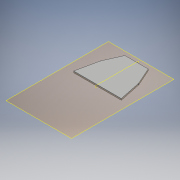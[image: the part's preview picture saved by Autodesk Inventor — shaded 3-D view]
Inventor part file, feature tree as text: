
AUTODESK INVENTOR PART (.ipt)
format: ipt  version: 2018 (Build 220112000, 112)  size: 160,256 bytes
history: native  units: mm
features: other x8, plane x1, sheet_metal_op x1, sketch x1, projected_geometry x1
ambient origin geometry x8: Origin, YZ Plane, XZ Plane, XY Plane, X Axis, Y Axis, Z Axis, Center Point
bodies: Solid1 (feature_tree)
feature tree (12):
  plane  "Work Plane1"
  sheet_metal_op  "Face1"
  other  "modplan parallel med plade"
  other  "midtplan"
  other  "Plate1"
  sketch  "Sketch3"  dims[d3=88.078826mm d4=44.039413mm d8=3.0mm d12=80.0mm d14=2.0mm d15=3.0mm d16=0.0mm]
  projected_geometry  "Projected Loop2"
  other  "2 mm mindre"
  parser-record x1  (decoder bookkeeping rows leaked as tree rows — omitted from the tree; the rows remain in map.json)
  other  "modul.iam"
  other  "stilladssøjle:1"
  other  "rør:1"
note: 1 file-system path scrubbed to <path> (originals preserved in map.json)
